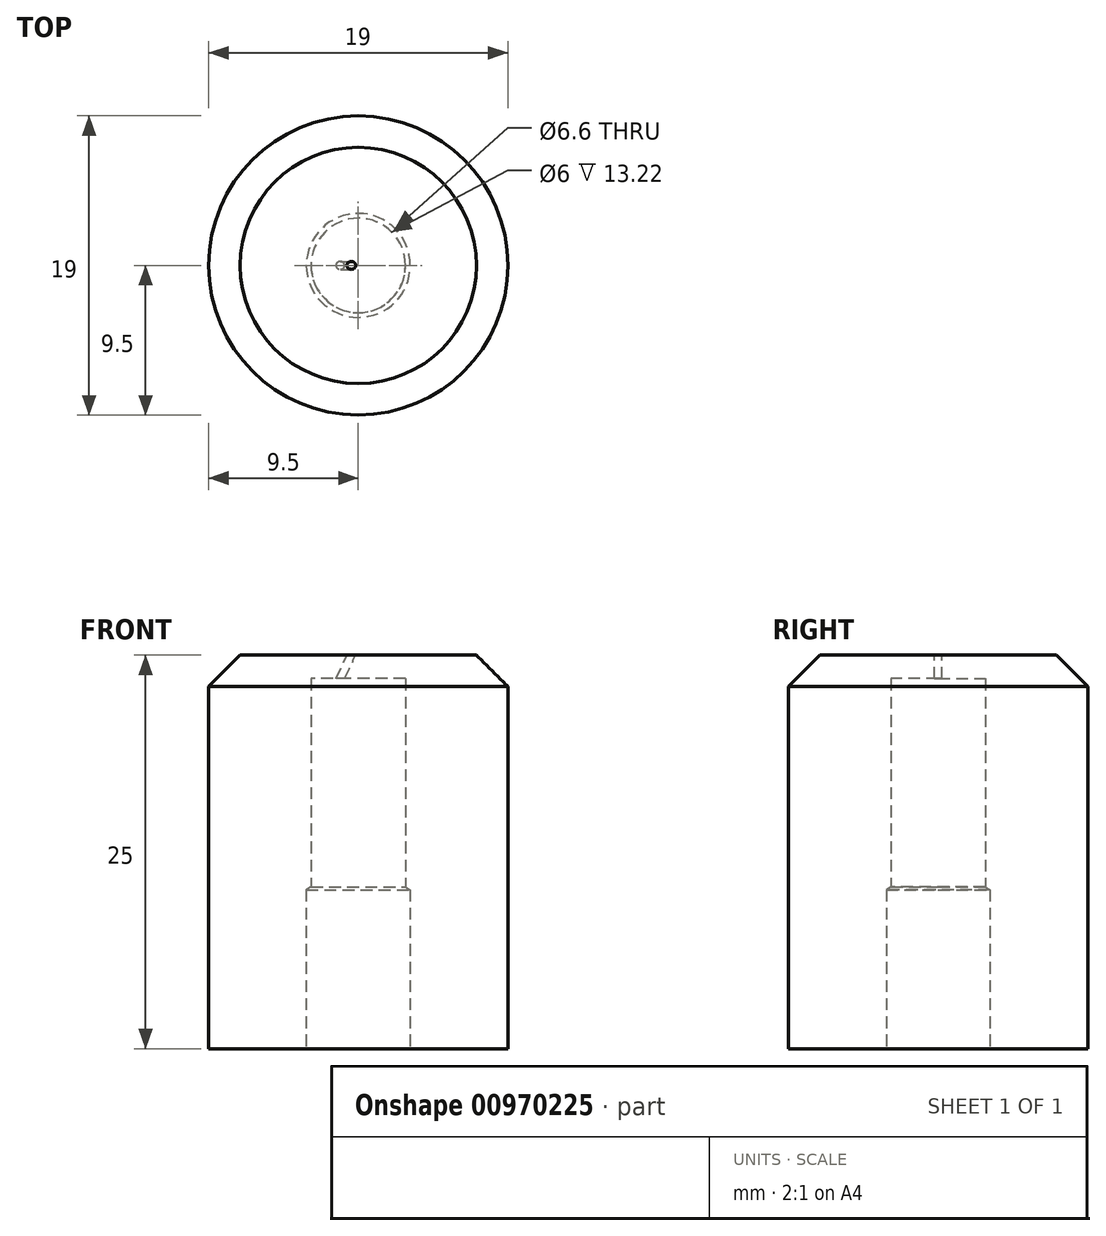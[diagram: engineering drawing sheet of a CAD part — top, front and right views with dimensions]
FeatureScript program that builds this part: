
annotation { "Feature Type Name" : "Feature", "Feature Type Description" : "" }
export const myFeature = defineFeature(function(context is Context, id is Id, definition is map)
    precondition{}
    {
        {
            var Q0;
            Q0=qCreatedBy(makeId("Top.planeOp"),FACE);
            var sketch = newSketch(context, id + "F0", { "sketchPlane" : qUnion([Q0])});
            skCircle(sketch, "E0", {"center": v(0, 0) * mm, "radius": 9.5 * mm});
            skSolve(sketch);
        }
        {
            var Q0;
            Q0 = qSketchRegion(id + "F0", true);
            extrude(context, id + "F1", {"entities" : qUnion([Q0]), "depth" : 25 * mm, "offsetDistance" : 25 * mm});
        }
        {
            var Q0;
            Q0=makeQuery(id+"F1.opExtrude","CAP_FACE",FACE,{"disambiguationData":[OSD([sQuery(id+"F0.wireOp",EDGE,"E0")])],"isStart":false});
            var sketch = newSketch(context, id + "F2", { "sketchPlane" : qUnion([Q0])});
            skLineSegment(sketch, "E1", {"start": v(0, -11.94) * mm, "end": v(0, 13.14) * mm, "construction": true});
            skSolve(sketch);
        }
        {
            var Q0;
            Q0=sQuery(id+"F2.wireOp",EDGE,"E1");
            cPlane(context, id + "F3", {"entities" : qUnion([Q0]), "cplaneType" : CPlaneType.LINE_ANGLE, "offset" : 25 * mm, "angle" : 25 * degree, "width" : 150 * mm, "height" : 150 * mm});
        }
        {
            var Q0;
            Q0=qCreatedBy(id+"F3.planeOp",FACE);
            var sketch = newSketch(context, id + "F4", { "sketchPlane" : qUnion([Q0])});
            skCircle(sketch, "E2", {"center": v(-10.97, 0) * mm, "radius": 0.25 * mm});
            skSolve(sketch);
        }
        {
            var Q0;
            Q0=qCreatedBy(makeId("Top.planeOp"),FACE);
            var sketch = newSketch(context, id + "F5", { "sketchPlane" : qUnion([Q0])});
            skCircle(sketch, "E3", {"center": v(0, 0) * mm, "radius": 3 * mm});
            skSolve(sketch);
        }
        {
            var Q0;
            Q0=makeQuery(id+"F1.opExtrude","CAP_EDGE",EDGE,{"disambiguationData":[OSD([sQuery(id+"F0.wireOp",EDGE,"E0")])],"isStart":false});
            chamfer(context, id + "F6", {"entities" : qUnion([Q0]), "width" : 2 * mm, "tangentPropagation" : true});
        }
        {
            var Q0;
            Q0=sQuery(id+"F5.wireOp",VERTEX,"E3.center");
            var Q1;
            Q1=makeQuery(id+"F1.opExtrude","SWEPT_BODY",BODY,{"disambiguationData":[OSD([sQuery(id+"F0.wireOp",EDGE,"E0")])]});
            hole(context, id + "F7", {"style" : HoleStyle.SIMPLE, "endStyle" : HoleEndStyle.BLIND, "oppositeDirection" : true, "standardTappedOrClearance" : lookupTablePath({ "fit" : "Normal", "standard" : "ISO", "size" : "M6", "type" : "Clearance" }), "standardBlindInLast" : lookupTablePath({ "fit" : "Normal", "standard" : "ISO", "engagement" : "75%", "pitch" : "1 mm", "size" : "M6", "type" : "Clearance & tapped" }), "holeDiameter" : 6.6 * mm, "majorDiameter" : 5 * mm, "holeDepth" : 10.1 * mm, "isTappedThrough" : true, "tappedDepth" : 12 * mm, "tapClearance" : 3, "locations" : qUnion([Q0]), "scope" : qUnion([Q1])});
        }
        {
            var Q0;
            Q0 = qSketchRegion(id + "F5", true);
            var Q1;
            Q1=makeQuery(id+"F1.opExtrude","CAP_FACE",FACE,{"disambiguationData":[OSD([sQuery(id+"F0.wireOp",EDGE,"E0")])],"isStart":false});
            extrude(context, id + "F8", {"entities" : qUnion([Q0]), "operationType" : NewBodyOperationType.REMOVE, "endBound" : BoundingType.UP_TO_SURFACE, "depth" : 25 * mm, "endBoundEntityFace" : qUnion([Q1]), "hasOffset" : true, "offsetDistance" : 1.5 * mm});
        }
        {
            var Q0;
            Q0 = qSketchRegion(id + "F4", true);
            var Q1;
            Q1=makeQuery(id+"F8.boolean.opBoolean","COPY",FACE,{"derivedFrom":makeQuery(id+"F8.opExtrude","CAP_FACE",FACE,{"disambiguationData":[OSD([sQuery(id+"F5.wireOp",EDGE,"E3")])],"isStart":false})});
            extrude(context, id + "F9", {"entities" : qUnion([Q0]), "operationType" : NewBodyOperationType.REMOVE, "endBound" : BoundingType.UP_TO_SURFACE, "oppositeDirection" : true, "depth" : 25 * mm, "endBoundEntityFace" : qUnion([Q1]), "offsetDistance" : 2 * mm, "offsetOppositeDirection" : true});
        }
    });
